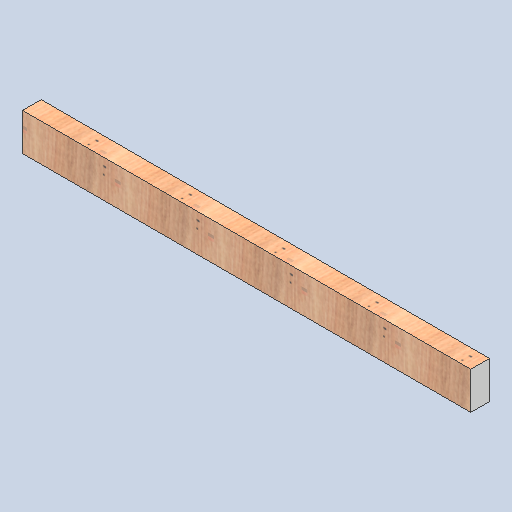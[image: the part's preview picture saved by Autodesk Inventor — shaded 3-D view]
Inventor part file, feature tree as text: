
AUTODESK INVENTOR PART (.ipt)
format: ipt  version: 2025 (Build 290162000, 162)  size: 148,992 bytes
history: native  units: in
note: dims shown in document units (in); Inventor stores cm internally (conversion verified against a paired STEP export)
features: other x3, sketch x2
ambient origin geometry x8: Origin, YZ Plane, XZ Plane, XY Plane, X Axis, Y Axis, Z Axis, Center Point
bodies: Solid1 (feature_tree)
feature tree (5):
  other  "2x4x48.ipt"
  other  "Solid1::2x4x48.ipt"
  other  "TaggingFeature1"
  sketch  "Sketch1"  dims[d0=0.3937in]
  sketch  "Sketch2"
